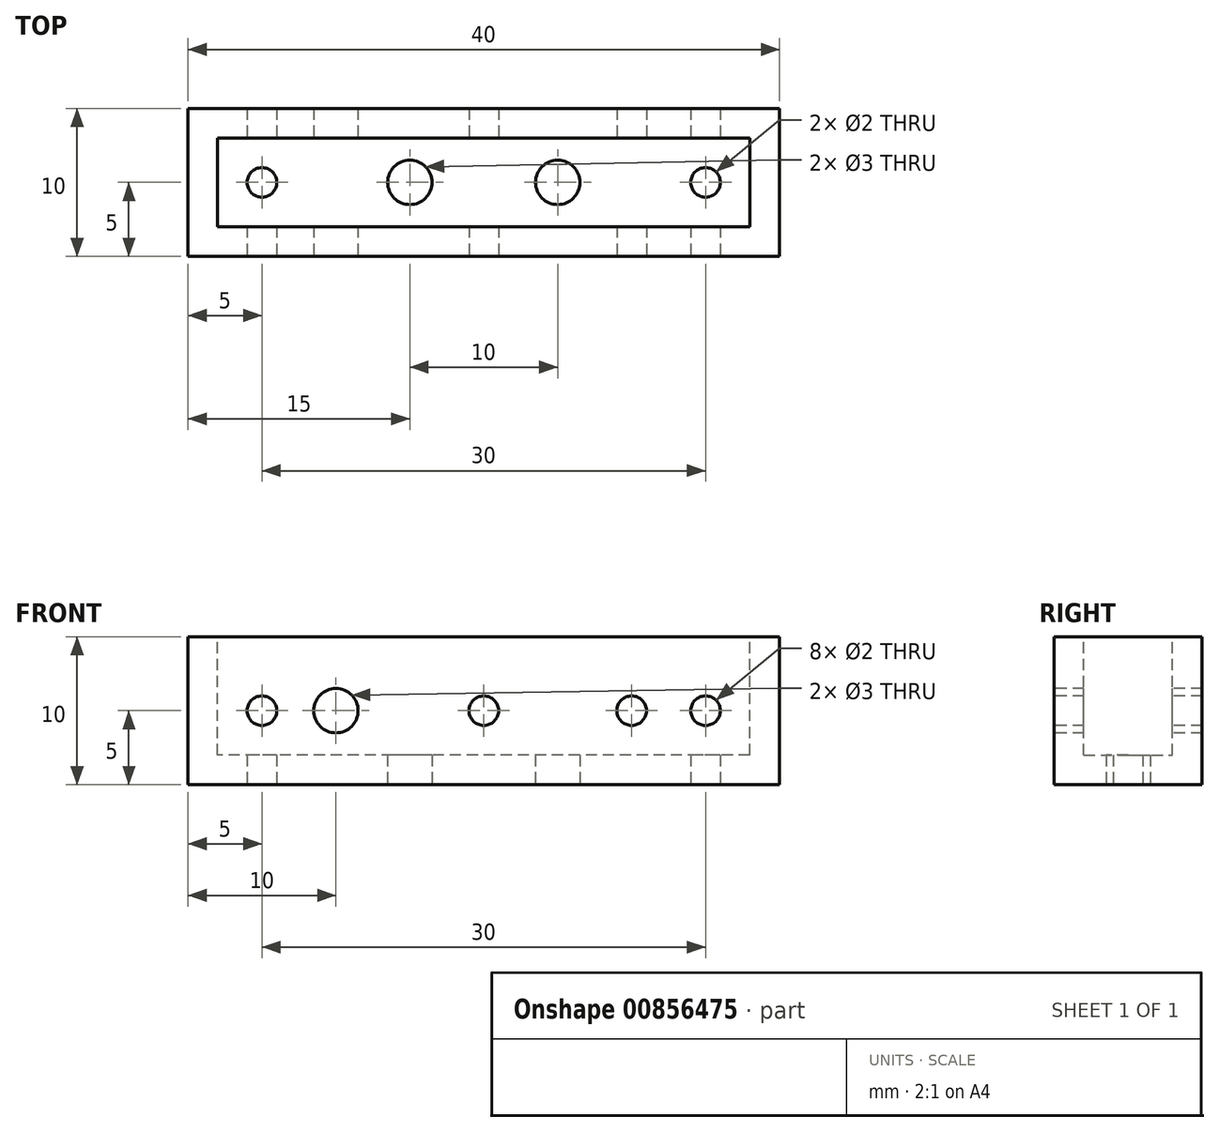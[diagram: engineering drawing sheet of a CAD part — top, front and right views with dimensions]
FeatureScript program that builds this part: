
annotation { "Feature Type Name" : "Feature", "Feature Type Description" : "" }
export const myFeature = defineFeature(function(context is Context, id is Id, definition is map)
    precondition{}
    {
        {
            var Q0;
            Q0=qCreatedBy(makeId("Top.planeOp"),FACE);
            var sketch = newSketch(context, id + "F0", { "sketchPlane" : qUnion([Q0])});
            skLineSegment(sketch, "E0.bottom", {"start": v(0, 0) * mm, "end": v(-40, 0) * mm});
            skLineSegment(sketch, "E0.top", {"start": v(0, 10) * mm, "end": v(-40, 10) * mm});
            skLineSegment(sketch, "E0.left", {"start": v(0, 0) * mm, "end": v(0, 10) * mm});
            skLineSegment(sketch, "E0.right", {"start": v(-40, 0) * mm, "end": v(-40, 10) * mm});
            skSolve(sketch);
        }
        {
            var Q0;
            Q0 = qSketchRegion(id + "F0", true);
            extrude(context, id + "F1", {"entities" : qUnion([Q0]), "depth" : 10 * mm, "offsetDistance" : 25 * mm});
        }
        {
            var Q0;
            Q0=makeQuery(id+"F1.opExtrude","CAP_FACE",FACE,{"disambiguationData":[OSD([sQuery(id+"F0.wireOp",EDGE,"E0.bottom"),sQuery(id+"F0.wireOp",EDGE,"E0.top"),sQuery(id+"F0.wireOp",EDGE,"E0.left"),sQuery(id+"F0.wireOp",EDGE,"E0.right")])],"isStart":true});
            var sketch = newSketch(context, id + "F2", { "sketchPlane" : qUnion([Q0])});
            skCircle(sketch, "E1", {"center": v(-35, -5) * mm, "radius": 1 * mm});
            skPoint(sketch, "E1.centerSnap0", {"position": v(-40, -5) * mm});
            skCircle(sketch, "E2", {"center": v(-5, -5) * mm, "radius": 1 * mm});
            skPoint(sketch, "E2.centerSnap0", {"position": v(0, -5) * mm});
            skCircle(sketch, "E3", {"center": v(-25, -5) * mm, "radius": 1.5 * mm});
            skCircle(sketch, "E4", {"center": v(-15, -5) * mm, "radius": 1.5 * mm});
            skSolve(sketch);
        }
        {
            var Q0;
            Q0 = qSketchRegion(id + "F2", true);
            extrude(context, id + "F3", {"entities" : qUnion([Q0]), "operationType" : NewBodyOperationType.REMOVE, "endBound" : BoundingType.THROUGH_ALL, "oppositeDirection" : true, "depth" : 25 * mm, "offsetDistance" : 25 * mm});
        }
        {
            var Q0;
            Q0=makeQuery(id+"F1.opExtrude","SWEPT_FACE",FACE,{"disambiguationData":[OSD([sQuery(id+"F0.wireOp",EDGE,"E0.bottom")])]});
            var sketch = newSketch(context, id + "F4", { "sketchPlane" : qUnion([Q0])});
            skCircle(sketch, "E5", {"center": v(-35, 5) * mm, "radius": 1 * mm});
            skPoint(sketch, "E5.centerSnap0", {"position": v(-40, 5) * mm});
            skCircle(sketch, "E6", {"center": v(-30, 5) * mm, "radius": 1.5 * mm});
            skCircle(sketch, "E7", {"center": v(-5, 5) * mm, "radius": 1 * mm});
            skPoint(sketch, "E7.centerSnap0", {"position": v(0, 5) * mm});
            skCircle(sketch, "E8", {"center": v(-10, 5) * mm, "radius": 1 * mm});
            skCircle(sketch, "E9", {"center": v(-20, 5) * mm, "radius": 1 * mm});
            skPoint(sketch, "E9.centerSnap0", {"position": v(-20, 10) * mm});
            skSolve(sketch);
        }
        {
            var Q0;
            Q0 = qSketchRegion(id + "F4", true);
            extrude(context, id + "F5", {"entities" : qUnion([Q0]), "operationType" : NewBodyOperationType.REMOVE, "endBound" : BoundingType.THROUGH_ALL, "oppositeDirection" : true, "depth" : 25 * mm, "offsetDistance" : 25 * mm});
        }
        {
            var Q0;
            Q0=makeQuery(id+"F1.opExtrude","CAP_FACE",FACE,{"disambiguationData":[OSD([sQuery(id+"F0.wireOp",EDGE,"E0.bottom"),sQuery(id+"F0.wireOp",EDGE,"E0.top"),sQuery(id+"F0.wireOp",EDGE,"E0.left"),sQuery(id+"F0.wireOp",EDGE,"E0.right")])],"isStart":false});
            var sketch = newSketch(context, id + "F6", { "sketchPlane" : qUnion([Q0])});
            skLineSegment(sketch, "E10.bottom", {"start": v(-38, 8) * mm, "end": v(-2, 8) * mm});
            skLineSegment(sketch, "E10.top", {"start": v(-38, 2) * mm, "end": v(-2, 2) * mm});
            skLineSegment(sketch, "E10.left", {"start": v(-38, 8) * mm, "end": v(-38, 2) * mm});
            skLineSegment(sketch, "E10.right", {"start": v(-2, 8) * mm, "end": v(-2, 2) * mm});
            skSolve(sketch);
        }
        {
            var Q0;
            Q0 = qSketchRegion(id + "F6", true);
            var Q1;
            Q1=makeQuery(id+"F1.opExtrude","CAP_FACE",FACE,{"disambiguationData":[OSD([sQuery(id+"F0.wireOp",EDGE,"E0.bottom"),sQuery(id+"F0.wireOp",EDGE,"E0.top"),sQuery(id+"F0.wireOp",EDGE,"E0.left"),sQuery(id+"F0.wireOp",EDGE,"E0.right")])],"isStart":true});
            extrude(context, id + "F7", {"entities" : qUnion([Q0]), "operationType" : NewBodyOperationType.REMOVE, "endBound" : BoundingType.UP_TO_SURFACE, "oppositeDirection" : true, "depth" : 25 * mm, "endBoundEntityFace" : qUnion([Q1]), "hasOffset" : true, "offsetDistance" : 2 * mm});
        }
    });
